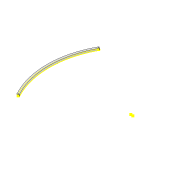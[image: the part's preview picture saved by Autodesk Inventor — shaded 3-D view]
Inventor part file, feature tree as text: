
AUTODESK INVENTOR PART (.ipt)
format: ipt  version: 2022 (Build 260153000, 153)  size: 108,544 bytes
history: native  units: mm
features: sketch x2, extrude x1, fillet x1, projected_geometry x1
ambient origin geometry x8: Origin, YZ Plane, XZ Plane, XY Plane, X Axis, Y Axis, Z Axis, Center Point
bodies: Solid1 (feature_tree)
feature tree (5):
  extrude  "Extrusion1"  Depth=10.0mm
  sketch  "Sketch2"  dims[d3=3.0mm d4=8.0mm d5=0.0mm d12=400.0mm d13=400.0mm d14=2.0mm]
  fillet  "Fillet1"  Radius=3.0mm
  sketch  "Sketch1"  dims[d0=382.775mm d1=10.0mm d2=3.0mm]
  projected_geometry  "Projected Loop1"
